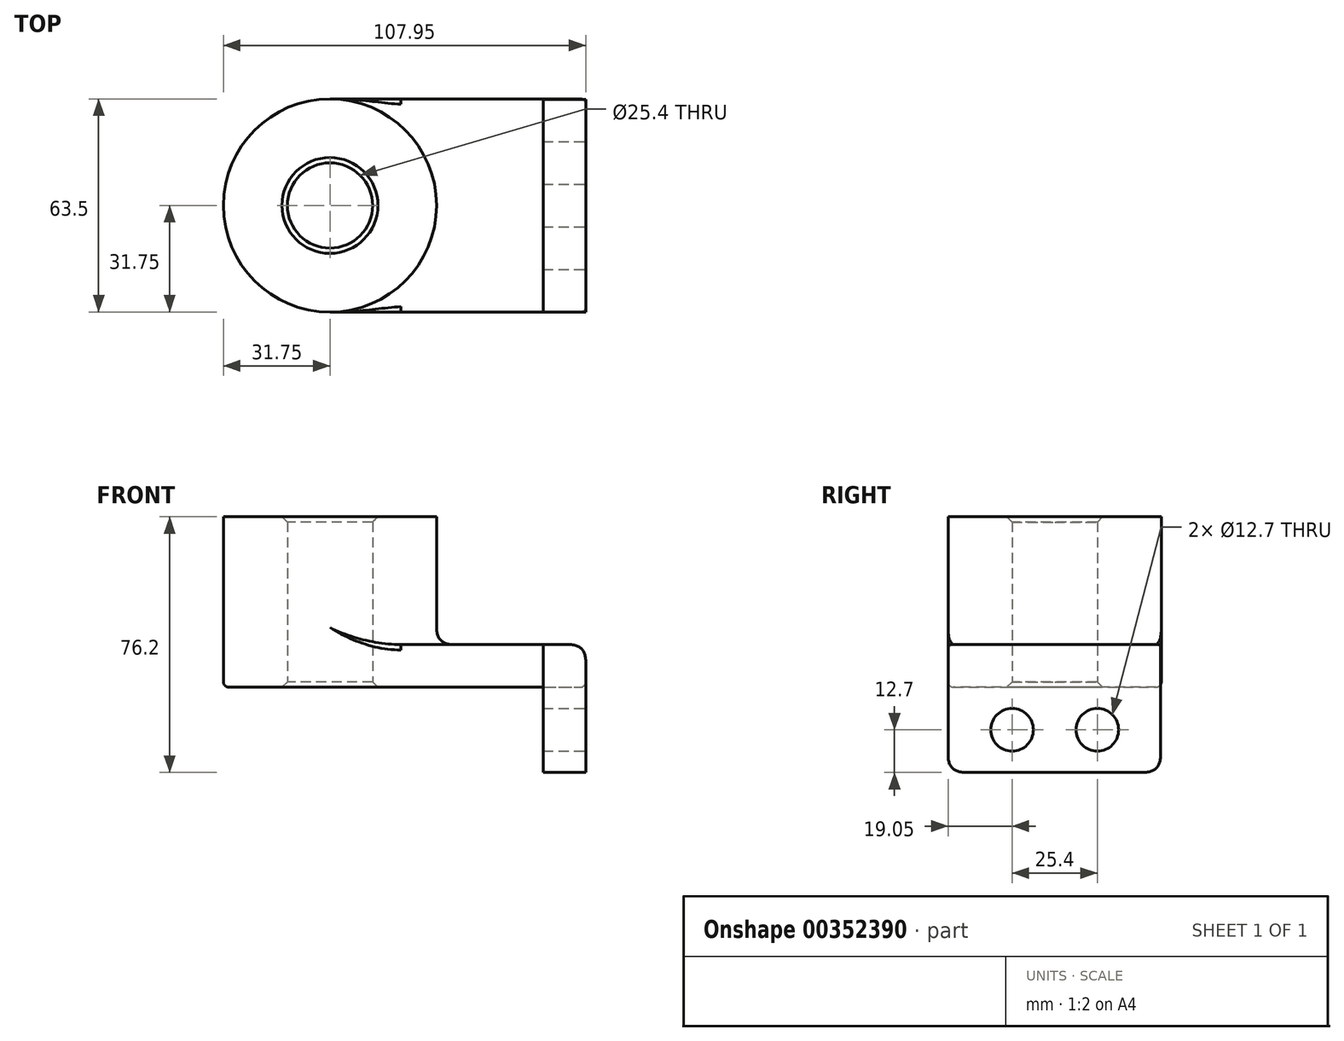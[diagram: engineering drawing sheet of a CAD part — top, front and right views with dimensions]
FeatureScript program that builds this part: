
annotation { "Feature Type Name" : "Feature", "Feature Type Description" : "" }
export const myFeature = defineFeature(function(context is Context, id is Id, definition is map)
    precondition{}
    {
        {
            var Q0;
            Q0=qCreatedBy(makeId("Top.planeOp"),FACE);
            var sketch = newSketch(context, id + "F0", { "sketchPlane" : qUnion([Q0])});
            skLineSegment(sketch, "E0.bottom", {"start": v(-38.1, -31.75) * mm, "end": v(38.1, -31.75) * mm});
            skLineSegment(sketch, "E0.top", {"start": v(-38.1, 31.75) * mm, "end": v(38.1, 31.75) * mm});
            skLineSegment(sketch, "E0.left", {"start": v(-38.1, -31.75) * mm, "end": v(-38.1, 31.75) * mm});
            skLineSegment(sketch, "E0.right", {"start": v(38.1, -31.75) * mm, "end": v(38.1, 31.75) * mm});
            skPoint(sketch, "E0.middle", {"position": v(0, 0) * mm});
            skCircle(sketch, "E1", {"center": v(-38.1, 0) * mm, "radius": 31.75 * mm});
            skCircle(sketch, "E2", {"center": v(-38.1, 0) * mm, "radius": 12.7 * mm});
            skSolve(sketch);
        }
        {
            var Q0;
            {var subQ0=sQuery(id+"F0.wireOp",EDGE,"E0.bottom");Q0=makeQuery(id+"F0.imprint","IMPRINT",FACE,{"disambiguationData":[TD([[makeQuery(id+"F0.imprint","IMPRINT",EDGE,{"derivedFrom":subQ0}),1.0]])]});}
            var Q1;
            {var subQ1=sQuery(id+"F0.wireOp",EDGE,"E0.left");var subQ3=sQuery(id+"F0.wireOp",EDGE,"E2");var subQ4=makeQuery(id+"F0.imprint","INTERSECT",VERTEX,{"disambiguationData":[OD(0.0)],"derivedFrom":[subQ1,subQ3]});Q1=makeQuery(id+"F0.imprint","IMPRINT",FACE,{"disambiguationData":[TD([[makeQuery(id+"F0.imprint","IMPRINT",EDGE,{"disambiguationData":[TD([[subQ4,1.0]])],"derivedFrom":subQ3}),-1.0]])]});}
            var Q2;
            {var subQ0=sQuery(id+"F0.wireOp",EDGE,"E2");var subQ1=sQuery(id+"F0.wireOp",EDGE,"E0.left");var subQ2=makeQuery(id+"F0.imprint","INTERSECT",VERTEX,{"disambiguationData":[OD(0.0)],"derivedFrom":[subQ1,subQ0]});Q2=makeQuery(id+"F0.imprint","IMPRINT",FACE,{"disambiguationData":[TD([[makeQuery(id+"F0.imprint","IMPRINT",EDGE,{"disambiguationData":[TD([[subQ2,-1.0]])],"derivedFrom":subQ1}),1.0]])]});}
            var Q3;
            {var subQ0=sQuery(id+"F0.wireOp",EDGE,"E2");var subQ1=sQuery(id+"F0.wireOp",EDGE,"E0.left");var subQ2=makeQuery(id+"F0.imprint","INTERSECT",VERTEX,{"disambiguationData":[OD(0.0)],"derivedFrom":[subQ1,subQ0]});Q3=makeQuery(id+"F0.imprint","IMPRINT",FACE,{"disambiguationData":[TD([[makeQuery(id+"F0.imprint","IMPRINT",EDGE,{"disambiguationData":[TD([[subQ2,-1.0]])],"derivedFrom":subQ1}),-1.0]])]});}
            var Q4;
            {var subQ1=sQuery(id+"F0.wireOp",EDGE,"E0.left");var subQ3=sQuery(id+"F0.wireOp",EDGE,"E2");var subQ4=makeQuery(id+"F0.imprint","INTERSECT",VERTEX,{"disambiguationData":[OD(0.0)],"derivedFrom":[subQ1,subQ3]});Q4=makeQuery(id+"F0.imprint","IMPRINT",FACE,{"disambiguationData":[TD([[makeQuery(id+"F0.imprint","IMPRINT",EDGE,{"disambiguationData":[TD([[subQ4,-1.0]])],"derivedFrom":subQ3}),-1.0]])]});}
            extrude(context, id + "F1", {"entities" : qUnion([Q0, Q1, Q2, Q3, Q4]), "depth" : 12.7 * mm});
        }
        {
            var Q0;
            {var subQ1=sQuery(id+"F0.wireOp",EDGE,"E0.left");var subQ3=sQuery(id+"F0.wireOp",EDGE,"E2");var subQ4=makeQuery(id+"F0.imprint","INTERSECT",VERTEX,{"disambiguationData":[OD(0.0)],"derivedFrom":[subQ1,subQ3]});Q0=makeQuery(id+"F0.imprint","IMPRINT",FACE,{"disambiguationData":[TD([[makeQuery(id+"F0.imprint","IMPRINT",EDGE,{"disambiguationData":[TD([[subQ4,1.0]])],"derivedFrom":subQ3}),-1.0]])]});}
            var Q1;
            {var subQ1=sQuery(id+"F0.wireOp",EDGE,"E0.left");var subQ3=sQuery(id+"F0.wireOp",EDGE,"E2");var subQ4=makeQuery(id+"F0.imprint","INTERSECT",VERTEX,{"disambiguationData":[OD(0.0)],"derivedFrom":[subQ1,subQ3]});Q1=makeQuery(id+"F0.imprint","IMPRINT",FACE,{"disambiguationData":[TD([[makeQuery(id+"F0.imprint","IMPRINT",EDGE,{"disambiguationData":[TD([[subQ4,-1.0]])],"derivedFrom":subQ3}),-1.0]])]});}
            extrude(context, id + "F2", {"entities" : qUnion([Q0, Q1]), "operationType" : NewBodyOperationType.ADD, "depth" : 50.8 * mm});
        }
        {
            var Q0;
            Q0=makeQuery(id+"F1.opExtrude","SWEPT_FACE",FACE,{"disambiguationData":[OSD([sQuery(id+"F0.wireOp",EDGE,"E0.right")])]});
            var sketch = newSketch(context, id + "F3", { "sketchPlane" : qUnion([Q0])});
            skLineSegment(sketch, "E3.bottom", {"start": v(-31.75, 12.7) * mm, "end": v(31.54, 12.7) * mm});
            skLineSegment(sketch, "E3.top", {"start": v(-31.75, -25.4) * mm, "end": v(31.54, -25.4) * mm});
            skLineSegment(sketch, "E3.left", {"start": v(-31.75, 12.7) * mm, "end": v(-31.75, -25.4) * mm});
            skLineSegment(sketch, "E3.right", {"start": v(31.54, 12.7) * mm, "end": v(31.54, -25.4) * mm});
            skCircle(sketch, "E4", {"center": v(-12.7, -12.7) * mm, "radius": 6.35 * mm});
            skLineSegment(sketch, "E5", {"start": v(0, 0) * mm, "end": v(0, -25.4) * mm, "construction": true});
            skCircle(sketch, "E6.MirrorC", {"center": v(12.7, -12.7) * mm, "radius": 6.35 * mm});
            skSolve(sketch);
        }
        {
            var Q0;
            {var subQ0=sQuery(id+"F3.wireOp",EDGE,"E3.bottom");Q0=makeQuery(id+"F3.imprint","IMPRINT",FACE,{"disambiguationData":[TD([[makeQuery(id+"F3.imprint","IMPRINT",EDGE,{"derivedFrom":subQ0}),-1.0]])]});}
            var Q1;
            {var subQ1=sQuery(id+"F3.wireOp",EDGE,"E3.top");Q1=makeQuery(id+"F3.imprint","IMPRINT",FACE,{"disambiguationData":[TD([[makeQuery(id+"F3.imprint","IMPRINT",EDGE,{"derivedFrom":subQ1}),1.0]])]});}
            extrude(context, id + "F4", {"entities" : qUnion([Q0, Q1]), "oppositeDirection" : true, "depth" : 12.7 * mm});
        }
        {
            var Q0;
            {var subQ0=sQuery(id+"F0.wireOp",EDGE,"E1");Q0=makeQuery(id+"F2.boolean.opBoolean","INTERSECT",EDGE,{"derivedFrom":[makeQuery(id+"F1.opExtrude","CAP_FACE",FACE,{"disambiguationData":[OSD([sQuery(id+"F0.wireOp",EDGE,"E0.bottom"),sQuery(id+"F0.wireOp",EDGE,"E0.top"),sQuery(id+"F0.wireOp",EDGE,"E0.right"),subQ0])],"isStart":false}),makeQuery(id+"F2.opExtrude","SWEPT_FACE",FACE,{"disambiguationData":[OSD([subQ0])]})]});}
            var Q1;
            Q1=makeQuery(id+"F4.opExtrude","CAP_EDGE",EDGE,{"disambiguationData":[OSD([sQuery(id+"F3.wireOp",EDGE,"E3.bottom")])],"isStart":true});
            var Q2;
            Q2=makeQuery(id+"F4.opExtrude","SWEPT_EDGE",EDGE,{"disambiguationData":[OSD([sQuery(id+"F3.wireOp",EDGE,"E3.top"),sQuery(id+"F3.wireOp",EDGE,"E3.left")])]});
            var Q3;
            Q3=makeQuery(id+"F4.opExtrude","SWEPT_EDGE",EDGE,{"disambiguationData":[OSD([sQuery(id+"F3.wireOp",EDGE,"E3.top"),sQuery(id+"F3.wireOp",EDGE,"E3.right")])]});
            var Q4;
            Q4=makeQuery(id+"F1.opExtrude","CAP_EDGE",EDGE,{"disambiguationData":[OSD([sQuery(id+"F0.wireOp",EDGE,"E0.right")])],"isStart":false});
            fillet(context, id + "F5", {"entities" : qUnion([Q0, Q1, Q2, Q3, Q4]), "radius" : 5.08 * mm, "tangentPropagation" : true, "rho" : 0.5, "crossSection" : FilletCrossSection.CONIC, "allowEdgeOverflow" : false});
        }
        {
            var Q0;
            Q0=makeQuery(id+"F1.opExtrude","CAP_EDGE",EDGE,{"disambiguationData":[OSD([sQuery(id+"F0.wireOp",EDGE,"E0.bottom")])],"isStart":false});
            var Q1;
            Q1=makeQuery(id+"F1.opExtrude","CAP_EDGE",EDGE,{"disambiguationData":[OSD([sQuery(id+"F0.wireOp",EDGE,"E0.bottom")])],"isStart":true});
            fillet(context, id + "F6", {"entities" : qUnion([Q0, Q1]), "radius" : 1.59 * mm, "tangentPropagation" : true, "allowEdgeOverflow" : false});
        }
        {
            var Q0;
            Q0=makeQuery(id+"F1.opExtrude","CAP_EDGE",EDGE,{"disambiguationData":[OSD([sQuery(id+"F0.wireOp",EDGE,"E0.top")])],"isStart":false});
            var Q1;
            {var subQ0=sQuery(id+"F0.wireOp",EDGE,"E0.top");Q1=makeQuery(id+"F6.opFillet","BLEND_EDGE",EDGE,{"blendedFrom":[makeQuery(id+"F1.opExtrude","CAP_EDGE",EDGE,{"disambiguationData":[OSD([subQ0])],"isStart":true}),makeQuery(id+"F1.opExtrude","SWEPT_FACE",FACE,{"disambiguationData":[OSD([subQ0])]})],"blendedInto":[makeQuery(id+"F1.opExtrude","SWEPT_FACE",FACE,{"disambiguationData":[OSD([subQ0])]})]});}
            fillet(context, id + "F7", {"entities" : qUnion([Q0, Q1]), "radius" : 1.59 * mm, "tangentPropagation" : true, "allowEdgeOverflow" : false});
        }
        {
            var Q0;
            Q0=makeQuery(id+"F2.opExtrude","SWEPT_FACE",FACE,{"disambiguationData":[OSD([sQuery(id+"F0.wireOp",EDGE,"E2")])]});
            chamfer(context, id + "F8", {"entities" : qUnion([Q0]), "width" : 1.59 * mm, "tangentPropagation" : true});
        }
    });
